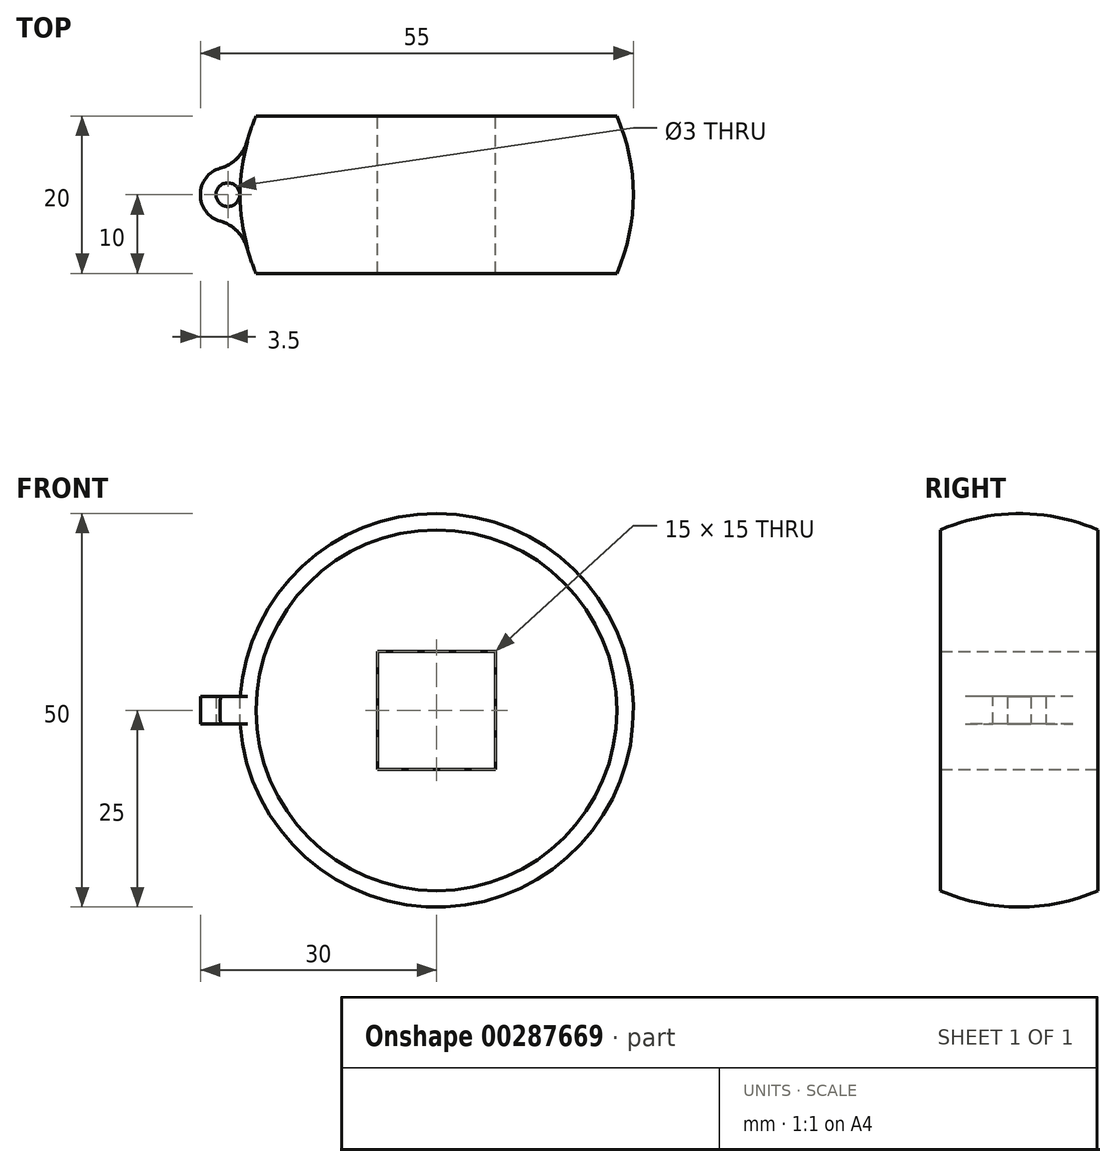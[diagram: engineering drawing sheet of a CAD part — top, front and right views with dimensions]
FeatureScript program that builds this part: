
annotation { "Feature Type Name" : "Feature", "Feature Type Description" : "" }
export const myFeature = defineFeature(function(context is Context, id is Id, definition is map)
    precondition{}
    {
        {
            var Q0;
            Q0=qCreatedBy(makeId("Front.planeOp"),FACE);
            var sketch = newSketch(context, id + "F0", { "sketchPlane" : qUnion([Q0])});
            skCircle(sketch, "E0", {"center": v(0, 0) * mm, "radius": 25 * mm});
            skSolve(sketch);
        }
        {
            var Q0;
            Q0=makeQuery(id+"F0.imprint","IMPRINT",FACE,{"disambiguationData":[TD([[makeQuery(id+"F0.imprint","IMPRINT",EDGE,{"derivedFrom":sQuery(id+"F0.wireOp",EDGE,"E0")}),1.0]])]});
            extrude(context, id + "F1", {"entities" : qUnion([Q0]), "endBound" : BoundingType.SYMMETRIC, "depth" : 20 * mm});
        }
        {
            var Q0;
            Q0=makeQuery(id+"F1.opExtrude","CAP_FACE",FACE,{"disambiguationData":[OSD([sQuery(id+"F0.wireOp",EDGE,"E0")])],"isStart":true});
            var sketch = newSketch(context, id + "F2", { "sketchPlane" : qUnion([Q0])});
            skLineSegment(sketch, "E1.bottom", {"start": v(7.5, 7.5) * mm, "end": v(-7.5, 7.5) * mm});
            skLineSegment(sketch, "E1.top", {"start": v(7.5, -7.5) * mm, "end": v(-7.5, -7.5) * mm});
            skLineSegment(sketch, "E1.left", {"start": v(7.5, 7.5) * mm, "end": v(7.5, -7.5) * mm});
            skLineSegment(sketch, "E1.right", {"start": v(-7.5, 7.5) * mm, "end": v(-7.5, -7.5) * mm});
            skPoint(sketch, "E1.middle", {"position": v(0, 0) * mm});
            skSolve(sketch);
        }
        {
            var Q0;
            Q0=makeQuery(id+"F2.imprint","IMPRINT",FACE,{"disambiguationData":[TD([[makeQuery(id+"F2.imprint","IMPRINT",EDGE,{"derivedFrom":sQuery(id+"F2.wireOp",EDGE,"E1.bottom")}),1.0]])]});
            extrude(context, id + "F3", {"entities" : qUnion([Q0]), "operationType" : NewBodyOperationType.REMOVE, "endBound" : BoundingType.THROUGH_ALL, "oppositeDirection" : true, "depth" : 17.8 * mm});
        }
        {
            var Q0;
            Q0=qCreatedBy(makeId("Right.planeOp"),FACE);
            var sketch = newSketch(context, id + "F4", { "sketchPlane" : qUnion([Q0])});
            skArc(sketch, "E2", {"start": v(10, 22.91) * mm, "mid": v(0, 25) * mm, "end": v(-10, 22.91) * mm});
            skLineSegment(sketch, "E3", {"start": v(-10, 22.91) * mm, "end": v(-10, 55) * mm});
            skLineSegment(sketch, "E4", {"start": v(10, 22.91) * mm, "end": v(10, 55) * mm});
            skLineSegment(sketch, "E5", {"start": v(10, 55) * mm, "end": v(-10, 55) * mm});
            skLineSegment(sketch, "E6", {"start": v(0, 0) * mm, "end": v(74.86, 0) * mm, "construction": true});
            skSolve(sketch);
        }
        {
            var Q0;
            Q0=makeQuery(id+"F4.imprint","IMPRINT",FACE,{"disambiguationData":[TD([[makeQuery(id+"F4.imprint","IMPRINT",EDGE,{"derivedFrom":sQuery(id+"F4.wireOp",EDGE,"E2")}),-1.0]])]});
            var Q1;
            Q1=sQuery(id+"F4.wireOp",EDGE,"E6");
            revolve(context, id + "F5", {"operationType" : NewBodyOperationType.REMOVE, "entities" : qUnion([Q0]), "axis" : qUnion([Q1]), "revolveType" : RevolveType.FULL, "oppositeDirection" : true});
        }
        {
            var Q0;
            Q0=qCreatedBy(makeId("Top.planeOp"),FACE);
            var sketch = newSketch(context, id + "F6", { "sketchPlane" : qUnion([Q0])});
            skCircle(sketch, "E7", {"center": v(-26.5, 0) * mm, "radius": 1.5 * mm});
            skCircle(sketch, "E8.0", {"center": v(-26.5, 0) * mm, "radius": 3.5 * mm});
            skArc(sketch, "E9", {"start": v(-22.91, 10) * mm, "mid": v(0, -25) * mm, "end": v(22.91, 10) * mm, "construction": true});
            skSolve(sketch);
        }
        {
            var Q0;
            Q0=makeQuery(id+"F6.imprint","IMPRINT",FACE,{"disambiguationData":[TD([[makeQuery(id+"F6.imprint","IMPRINT",EDGE,{"derivedFrom":sQuery(id+"F6.wireOp",EDGE,"E7")}),-1.0]])]});
            extrude(context, id + "F7", {"entities" : qUnion([Q0]), "operationType" : NewBodyOperationType.ADD, "endBound" : BoundingType.SYMMETRIC, "depth" : 3.5 * mm});
        }
        {
            var Q0;
            Q0=makeQuery(id+"F7.boolean.opBoolean","INTERSECT",EDGE,{"disambiguationData":[OD(0.0)],"derivedFrom":[makeQuery(id+"F5.boolean.opBoolean","COPY",FACE,{"derivedFrom":makeQuery(id+"F5.opRevolve","SWEPT_FACE",FACE,{"disambiguationData":[OSD([sQuery(id+"F4.wireOp",EDGE,"E2")])]})}),makeQuery(id+"F7.opExtrude","SWEPT_FACE",FACE,{"disambiguationData":[OSD([sQuery(id+"F6.wireOp",EDGE,"E8.0")])]})]});
            var Q1;
            Q1=makeQuery(id+"F7.boolean.opBoolean","INTERSECT",EDGE,{"disambiguationData":[OD(1.0)],"derivedFrom":[makeQuery(id+"F5.boolean.opBoolean","COPY",FACE,{"derivedFrom":makeQuery(id+"F5.opRevolve","SWEPT_FACE",FACE,{"disambiguationData":[OSD([sQuery(id+"F4.wireOp",EDGE,"E2")])]})}),makeQuery(id+"F7.opExtrude","SWEPT_FACE",FACE,{"disambiguationData":[OSD([sQuery(id+"F6.wireOp",EDGE,"E8.0")])]})]});
            fillet(context, id + "F8", {"entities" : qUnion([Q0, Q1]), "radius" : 5 * mm, "tangentPropagation" : true, "allowEdgeOverflow" : false});
        }
    });
